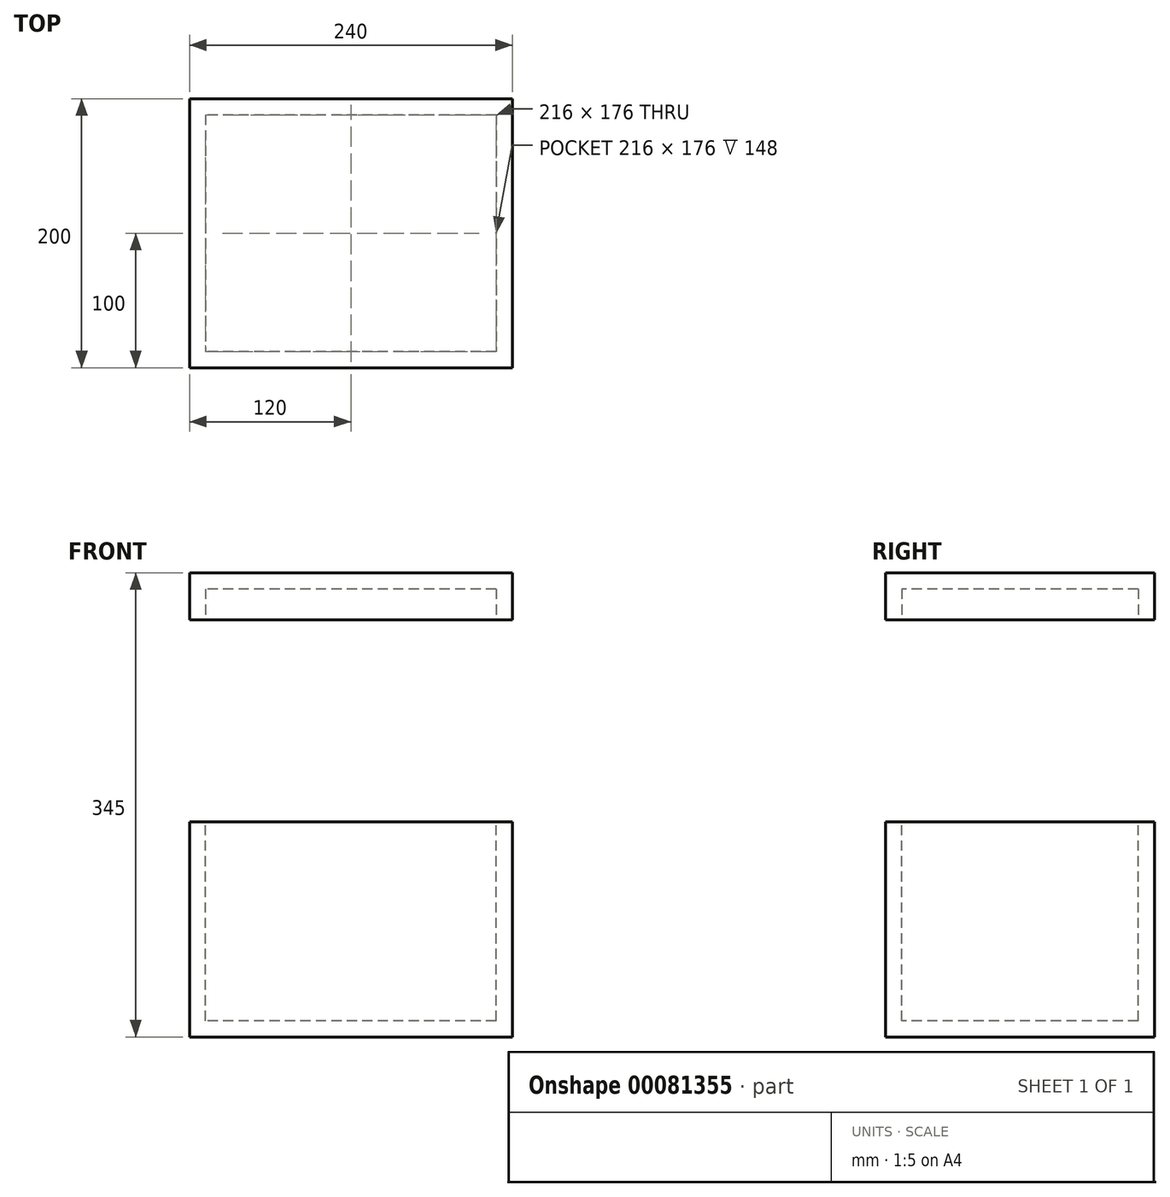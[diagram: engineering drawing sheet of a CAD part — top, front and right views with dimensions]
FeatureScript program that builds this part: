
annotation { "Feature Type Name" : "Feature", "Feature Type Description" : "" }
export const myFeature = defineFeature(function(context is Context, id is Id, definition is map)
    precondition{}
    {
        {
            var Q0;
            Q0=qCreatedBy(makeId("Top.planeOp"),FACE);
            var sketch = newSketch(context, id + "F0", { "sketchPlane" : qUnion([Q0])});
            skLineSegment(sketch, "E0.bottom", {"start": v(120, 100) * mm, "end": v(-120, 100) * mm});
            skLineSegment(sketch, "E0.top", {"start": v(120, -100) * mm, "end": v(-120, -100) * mm});
            skLineSegment(sketch, "E0.left", {"start": v(120, 100) * mm, "end": v(120, -100) * mm});
            skLineSegment(sketch, "E0.right", {"start": v(-120, 100) * mm, "end": v(-120, -100) * mm});
            skPoint(sketch, "E0.middle", {"position": v(0, 0) * mm});
            skSolve(sketch);
        }
        {
            var Q0;
            Q0=makeQuery(id+"F0.imprint","IMPRINT",FACE,{"disambiguationData":[TD([[makeQuery(id+"F0.imprint","IMPRINT",EDGE,{"derivedFrom":sQuery(id+"F0.wireOp",EDGE,"E0.bottom")}),1.0]])]});
            extrude(context, id + "F1", {"entities" : qUnion([Q0]), "oppositeDirection" : true, "depth" : 160 * mm});
        }
        {
            var Q0;
            Q0=makeQuery(id+"F1.opExtrude","CAP_FACE",FACE,{"disambiguationData":[OSD([sQuery(id+"F0.wireOp",EDGE,"E0.bottom"),sQuery(id+"F0.wireOp",EDGE,"E0.top"),sQuery(id+"F0.wireOp",EDGE,"E0.left"),sQuery(id+"F0.wireOp",EDGE,"E0.right")])],"isStart":true});
            shell(context, id + "F2", {"entities" : qUnion([Q0]), "thickness" : 12 * mm});
        }
        {
            var Q0;
            Q0=makeQuery(id+"F1.opExtrude","CAP_FACE",FACE,{"disambiguationData":[OSD([sQuery(id+"F0.wireOp",EDGE,"E0.bottom"),sQuery(id+"F0.wireOp",EDGE,"E0.top"),sQuery(id+"F0.wireOp",EDGE,"E0.left"),sQuery(id+"F0.wireOp",EDGE,"E0.right")])],"isStart":true});
            cPlane(context, id + "F3", {"entities" : qUnion([Q0]), "cplaneType" : CPlaneType.OFFSET, "offset" : 150 * mm, "width" : 150 * mm, "height" : 150 * mm});
        }
        {
            var Q0;
            Q0=qCreatedBy(id+"F3.planeOp",FACE);
            var sketch = newSketch(context, id + "F4", { "sketchPlane" : qUnion([Q0])});
            skLineSegment(sketch, "E1.bottom", {"start": v(120, 100) * mm, "end": v(-120, 100) * mm});
            skLineSegment(sketch, "E1.top", {"start": v(120, -100) * mm, "end": v(-120, -100) * mm});
            skLineSegment(sketch, "E1.left", {"start": v(120, 100) * mm, "end": v(120, -100) * mm});
            skLineSegment(sketch, "E1.right", {"start": v(-120, 100) * mm, "end": v(-120, -100) * mm});
            skPoint(sketch, "E1.middle", {"position": v(0, 0) * mm});
            skSolve(sketch);
        }
        {
            var Q0;
            Q0=makeQuery(id+"F4.imprint","IMPRINT",FACE,{"disambiguationData":[TD([[makeQuery(id+"F4.imprint","IMPRINT",EDGE,{"derivedFrom":sQuery(id+"F4.wireOp",EDGE,"E1.bottom")}),1.0]])]});
            extrude(context, id + "F5", {"entities" : qUnion([Q0]), "depth" : 35 * mm});
        }
        {
            var Q0;
            Q0=makeQuery(id+"F5.opExtrude","CAP_FACE",FACE,{"disambiguationData":[OSD([sQuery(id+"F4.wireOp",EDGE,"E1.bottom"),sQuery(id+"F4.wireOp",EDGE,"E1.top"),sQuery(id+"F4.wireOp",EDGE,"E1.left"),sQuery(id+"F4.wireOp",EDGE,"E1.right")])],"isStart":true});
            shell(context, id + "F6", {"entities" : qUnion([Q0]), "thickness" : 12 * mm});
        }
    });
